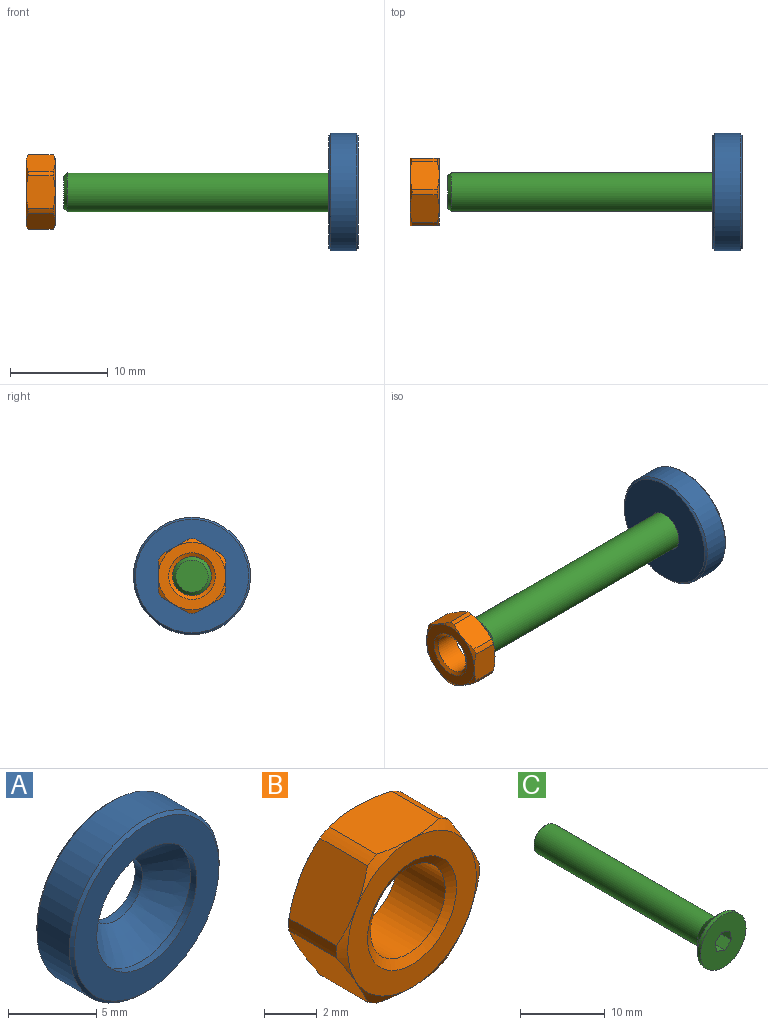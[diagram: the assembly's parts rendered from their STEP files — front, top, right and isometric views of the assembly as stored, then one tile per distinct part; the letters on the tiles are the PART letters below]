
ASSEMBLY  parts=3 mates=2
PART A: 8 faces, bbox 12x3x12 mm
  f0: cylinder r=2.08mm len=4.15mm, axis (0,1,0), area 7.5mm2, adj f3,f4
  f1: cylinder r=6mm len=12mm, axis (0,1,0), area 98mm2, adj f6,f7
  f2: plane 11.6x11.6mm, normal (0,-1,0), area 55.4mm2, adj f5,f7
  f3: plane 11.6x11.6mm, normal (0,1,0), area 92.2mm2, adj f0,f6
  f4: cone r=4mm half-angle=45deg, axis (0,-1,0), area 52mm2, adj f0,f5
  f5: cylinder r=4mm len=8mm, axis (0,-1,0), area 12.6mm2, adj f2,f4
  f6: cone r=6mm half-angle=45deg, axis (0,-1,0), area 10.5mm2, adj f1,f3
  f7: cone r=5.8mm half-angle=45deg, axis (0,1,0), area 10.5mm2, adj f1,f2
PART B: 19 faces, bbox 7.7x3x7.7 mm
  f0: cylinder r=3.83mm len=2.56mm, axis (0,-1,0), area 1.5mm2, adj f11,f12,f17,f18
  f1: cylinder r=3.83mm len=2.56mm, axis (0,-1,0), area 1.5mm2, adj f11,f12,f16,f17
  f2: cylinder r=3.83mm len=2.56mm, axis (0,-1,0), area 1.5mm2, adj f11,f12,f15,f16
  f3: cylinder r=3.83mm len=2.56mm, axis (0,-1,0), area 1.5mm2, adj f11,f12,f14,f15
  f4: cylinder r=3.83mm len=2.56mm, axis (0,-1,0), area 1.5mm2, adj f11,f12,f13,f14
  f5: cylinder r=2mm len=4mm, axis (0,-1,0), area 32.1mm2, adj f9,f10
  f6: plane 6.89x6.89mm, normal (0,1,0), area 19.4mm2, adj f9,f11
  f7: cylinder r=3.83mm len=2.56mm, axis (0,-1,0), area 1.5mm2, adj f11,f12,f13,f18
  f8: plane 6.89x6.89mm, normal (0,-1,0), area 19.4mm2, adj f10,f12
  f9: cone r=2.38mm half-angle=60deg, axis (0,1,0), area 6.1mm2, adj f5,f6
  f10: cone r=2mm half-angle=60deg, axis (0,-1,0), area 6.1mm2, adj f5,f8
  f11: cone r=3.83mm half-angle=60deg, axis (0,-1,0), area 4.3mm2, adj f0,f1,f2,f3,f4,f6,f7,f13
  f12: cone r=3.45mm half-angle=60deg, axis (0,1,0), area 4.3mm2, adj f0,f1,f2,f3,f4,f7,f8,f13
  f13: plane 3x2.88mm, normal (-0.87,0,0.5), area 9.5mm2, adj f4,f7,f11,f12
  f14: plane 3x2.88mm, normal (-0.87,0,-0.5), area 9.5mm2, adj f3,f4,f11,f12
  f15: plane 3.33x3mm, normal (0,0,-1), area 9.5mm2, adj f2,f3,f11,f12
  f16: plane 3x2.88mm, normal (0.87,0,-0.5), area 9.5mm2, adj f1,f2,f11,f12
  f17: plane 3x2.88mm, normal (0.87,0,0.5), area 9.5mm2, adj f0,f1,f11,f12
  f18: plane 3.33x3mm, normal (0,0,1), area 9.5mm2, adj f0,f7,f11,f12
PART C: 13 faces, bbox 7.6x30x7.6 mm
  f0: plane 7.6x7.6mm, normal (0,-1,0), area 40mm2, adj f5,f6,f7,f8,f9,f10,f11
  f1: plane 3.29x3.29mm, normal (0,1,0), area 8.5mm2, adj f2
  f2: cone r=2mm half-angle=45deg, axis (0,-1,0), area 5.7mm2, adj f1,f3
  f3: cylinder r=2mm len=27.35mm, axis (0,1,0), area 343.6mm2, adj f2,f4
  f4: cone r=3.8mm half-angle=45deg, axis (0,-1,0), area 46.4mm2, adj f3,f5
  f5: cylinder r=3.8mm len=7.6mm, axis (0,1,0), area 11.9mm2, adj f0,f4
  f6: plane 1.8x1.1mm, normal (0.65,0,-0.76), area 2.6mm2, adj f0,f7,f11,f12
  f7: plane 1.8x1.42mm, normal (0.98,0,0.18), area 2.6mm2, adj f0,f6,f8,f12
  f8: plane 1.8x1.36mm, normal (0.33,0,0.94), area 2.6mm2, adj f0,f7,f9,f12
  f9: plane 1.8x1.1mm, normal (-0.65,0,0.76), area 2.6mm2, adj f0,f8,f10,f12
  f10: plane 1.8x1.42mm, normal (-0.98,0,-0.18), area 2.6mm2, adj f0,f9,f11,f12
  f11: plane 1.8x1.36mm, normal (-0.33,0,-0.94), area 2.6mm2, adj f0,f6,f10,f12
  f12: plane 2.84x2.72mm, normal (0,-1,0), area 5.4mm2, adj f6,f7,f8,f9,f10,f11
PLACE A rot(axis=(0.71,-0.71,0),180deg) t=(7.15,24.48,86.05)mm
PLACE B rot(axis=(-0.58,0.58,0.58),120deg) t=(-23.35,39.15,98)mm
PLACE C rot(axis=(0.71,-0.71,0),180deg) t=(-3.9,132.15,98)mm
MATE fastened B.f0 <-> A.f0  axis (1,0,0) through (-23.35,39.15,98)mm
MATE fastened A.f0 <-> C.f2  axis (1,0,0) through (5.22,39.15,98)mm
